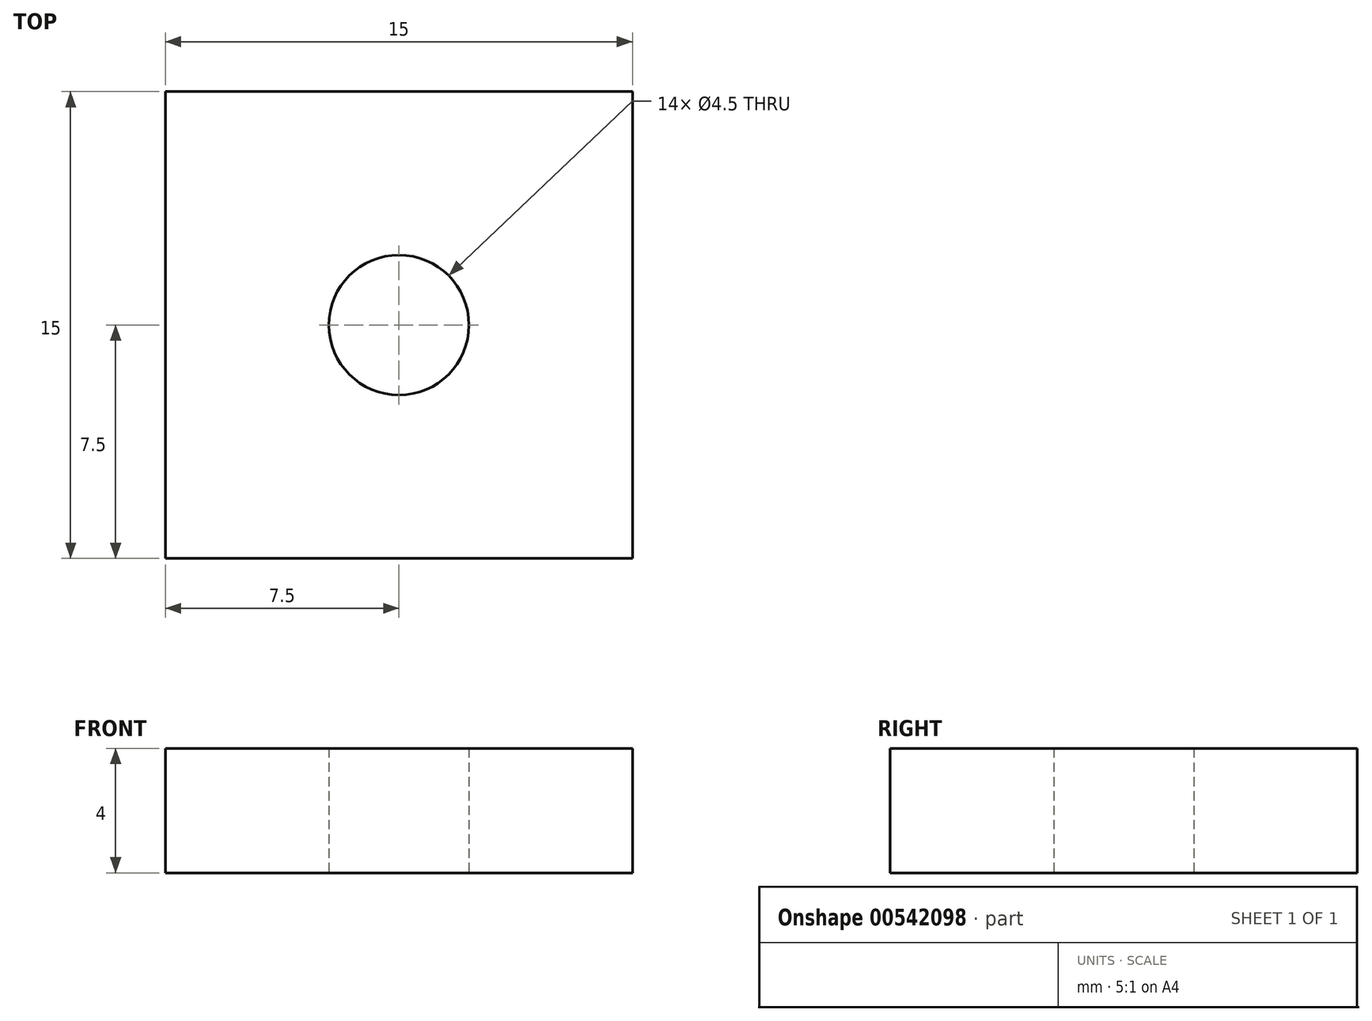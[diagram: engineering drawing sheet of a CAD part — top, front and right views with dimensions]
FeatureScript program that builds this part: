
annotation { "Feature Type Name" : "Feature", "Feature Type Description" : "" }
export const myFeature = defineFeature(function(context is Context, id is Id, definition is map)
    precondition{}
    {
        {
            var Q0;
            Q0=qCreatedBy(makeId("Top.planeOp"),FACE);
            var sketch = newSketch(context, id + "F0", { "sketchPlane" : qUnion([Q0])});
            skLineSegment(sketch, "E0.bottom", {"start": v(7.5, -7.5) * mm, "end": v(-7.5, -7.5) * mm});
            skLineSegment(sketch, "E0.top", {"start": v(7.5, 7.5) * mm, "end": v(-7.5, 7.5) * mm});
            skLineSegment(sketch, "E0.left", {"start": v(7.5, -7.5) * mm, "end": v(7.5, 7.5) * mm});
            skLineSegment(sketch, "E0.right", {"start": v(-7.5, -7.5) * mm, "end": v(-7.5, 7.5) * mm});
            skPoint(sketch, "E0.middle", {"position": v(0, 0) * mm});
            skCircle(sketch, "E1", {"center": v(0, 0) * mm, "radius": 2.25 * mm});
            skSolve(sketch);
        }
        {
            var Q0;
            Q0=makeQuery(id+"F0.imprint","IMPRINT",FACE,{"disambiguationData":[TD([[makeQuery(id+"F0.imprint","IMPRINT",EDGE,{"derivedFrom":sQuery(id+"F0.wireOp",EDGE,"E0.bottom")}),-1.0]])]});
            extrude(context, id + "F1", {"entities" : qUnion([Q0]), "depth" : 4 * mm, "offsetDistance" : 25 * mm});
        }
    });
